# Revit family: Legrand_Lighting_Management_SCS_Actuator
name_source: partatom
category: Dispositifs d'éclairage
units: mm (PartAtom-declared; Revit-internal decimal feet)

## family parameters
Conserver l'orientation des annotations = Non
Cote de connecteur circulaire = Utiliser le diamètre
Couper avec des vides une fois chargée = Non
Hôte = Face
Partagée = Non
Point de calcul de pièce = Non
Type d'élément = Normal

## types (6) — shared parameters
Alarm function = Non
Collecteur de terre = Non
Colour = <Par catégorie>
Constant light control = Non
Cosses d'artère secondaire = Non
Degree of protection (IP) = IP20
Dim function with dimmer basic element = Non
Elévation par défaut = 1219 mm
Fabricant = Legrand
Forced switch off = Non
General Conditions of Use = https://export.legrand.com
HVAC-control = Non
Liaison neutre = Non
Remote operation = Non
Response value luminosity adjustable = Non
Response value sensitivity adjustable = Non
Suitable for wireless transmission = Non
URL = http://www.legrandoc.com
zero-valued in all types: Detection angle horizontal (MAX) (°), Detection angle horizontal (MIN) (°), Diameter detection range on floor (m), Max. duty cycle (mn), Max. starting current (A), Max. transmission range frontally (m), Max. transmission range sideways (m), Maximum mounting height (m), Min. switch-on time (s), Nominal voltage (V), RAL-number (akin), Response value luminosity (MAX) (lx), Response value luminosity (MIN) (lx), Temperature (MAX) (°C), Temperature (MIN) (°C)

## per-type parameters (varying)
| type | Description | Frequency (MAX) (Hz) | Frequency (MIN) (Hz) | Max. switching power (W) | Model | Modèle | Mounting method | Multi applications 2 sorties éclairage, 1 sortie volet et 1 sortie VMC | ON/OFF 2 sorties 16A | Substation input | Types de modélisations | Variation 0-10V 2 sorties | Variation 0-10V 4 sorties | Variation DALI 4 sorties |
| ON/OFF 2 outputs 16A | Lighting management-room controller ON/OFF-ceiling mounting-2 outputs-16 A | 0 | 0 | 3680 |  | 048841 | Wall duct | Non | Oui | Non | Modelisation 84 : Ref 048841 | Non | Non | Non |
| Dimming 0-10V 2 outputs | Lighting management-dimmer room controller-ceiling mounting-2 outputs 0/10 V | 60 | 50 | 0 | Control module | 048842 | Surface mounted (plaster) | Non | Non | Oui | Modelisation 84 : Ref 048842 | Oui | Non | Non |
| Dimming 0-10V 4 outputs | Lighting management-dimmer room controller-ceiling mounting-4 outputs 0/10 V | 60 | 50 | 0 | Control module | 048843 | Surface mounted (plaster) | Non | Non | Oui | Modelisation 85 | Non | Oui | Non |
| Dimming DALI 4 outputs | Lighting management-dimmer room controller-8 outputs for DALI ballasts | 60 | 50 | 0 | Control module | 048844 | Surface mounted (plaster) | Non | Non | Oui | Modelisation 85 | Non | Non | Oui |
| Multi app 2 light output, 1 shutter output, 1 CMV output | Lighting management-room controller ON/OFF-2 outputs blind/shutter control-16 A | 60 | 50 | 0 | Control module | 048847 | Other | Oui | Non | Non | Modelisation 85 | Non | Non | Non |
| Halogen Dimming BT/TBT 2 outputs | Lighting management-dimmer room controller-ceiling mounting-2 outputs all load | 60 | 50 | 0 | Control module | 048845 | Surface mounted (plaster) | Non | Non | Oui | Modelisation 86 | Non | Non | Non |
